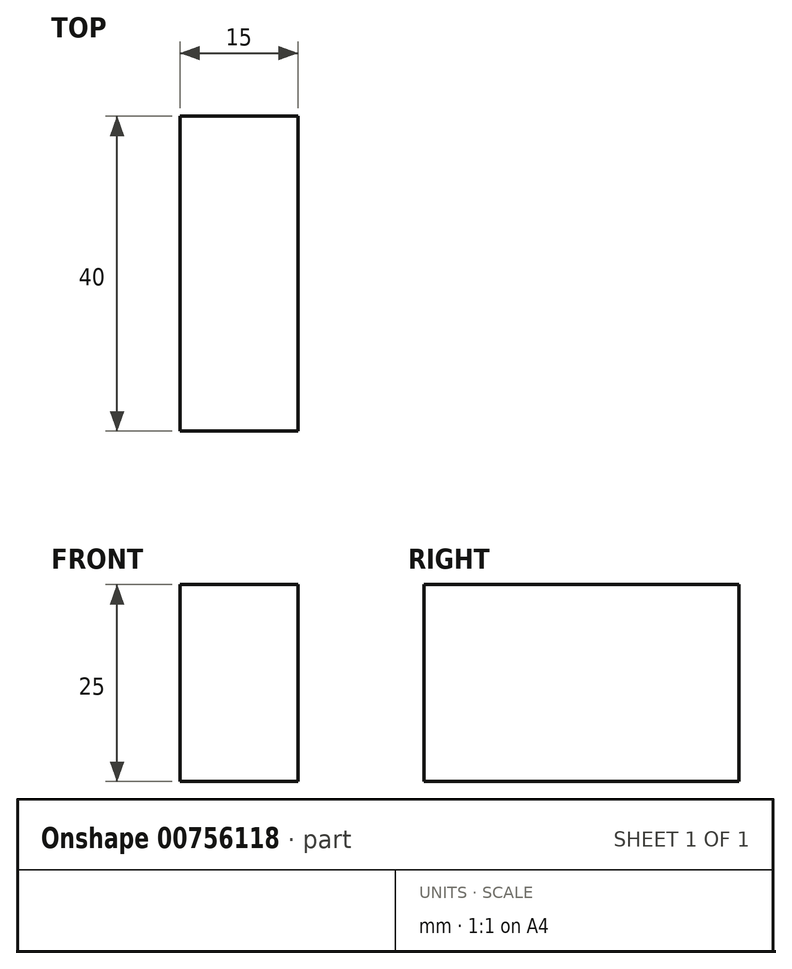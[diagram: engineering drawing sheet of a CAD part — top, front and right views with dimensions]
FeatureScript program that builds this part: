
annotation { "Feature Type Name" : "Feature", "Feature Type Description" : "" }
export const myFeature = defineFeature(function(context is Context, id is Id, definition is map)
    precondition{}
    {
        {
            var Q0;
            Q0=qCreatedBy(makeId("Top.planeOp"),FACE);
            var sketch = newSketch(context, id + "F0", { "sketchPlane" : qUnion([Q0])});
            skLineSegment(sketch, "E0.bottom", {"start": v(-7.5, -20) * mm, "end": v(7.5, -20) * mm});
            skLineSegment(sketch, "E0.top", {"start": v(-7.5, 20) * mm, "end": v(7.5, 20) * mm});
            skLineSegment(sketch, "E0.left", {"start": v(-7.5, -20) * mm, "end": v(-7.5, 20) * mm});
            skLineSegment(sketch, "E0.right", {"start": v(7.5, -20) * mm, "end": v(7.5, 20) * mm});
            skPoint(sketch, "E0.middle", {"position": v(0, 0) * mm});
            skSolve(sketch);
        }
        {
            var Q0;
            Q0 = qSketchRegion(id + "F0", true);
            extrude(context, id + "F1", {"entities" : qUnion([Q0]), "depth" : 25 * mm, "offsetDistance" : 25 * mm});
        }
    });
